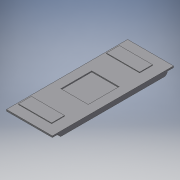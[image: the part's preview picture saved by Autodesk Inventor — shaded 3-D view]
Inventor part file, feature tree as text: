
AUTODESK INVENTOR PART (.ipt)
format: ipt  version: 2016 SP2 (Build 200236200, 236)  size: 184,320 bytes
history: native  units: mm
features: extrude x5, sketch x5, chamfer x1, reference x1
ambient origin geometry x8: Origin, YZ Plane, XZ Plane, XY Plane, X Axis, Y Axis, Z Axis, Center Point
bodies: Volumenkörper1 (feature_tree)
feature tree (12):
  extrude  "Extrusion1"  Depth=24.9mm
  extrude  "Extrusion2"  Depth=3.5mm
  extrude  "Extrusion3"  Depth=0.8mm TaperAngle=0.0deg
  chamfer  "Fase1"  Distance=7.0mm
  extrude  "Extrusion4"  Depth=7.0mm
  extrude  "Extrusion5"  Depth=5.5mm
  sketch  "Skizze1"  dims[d0=0.1mm d1=24.9mm]
  reference  "Referenz1"
  sketch  "Skizze2"  dims[d2=1.8mm d3=0.0mm d4=3.5mm]
  sketch  "Skizze3"  dims[d5=3.5mm d6=0.8mm d7=0.0mm]
  sketch  "Skizze4"  dims[d8=18.0mm]
  sketch  "Skizze5"  dims[d9=18.0mm d10=7.0mm d11=7.0mm d12=5.5mm d13=5.5mm d14=1.0mm d15=0.4mm d16=0.0mm d17=1.0mm d18=2.0mm d19=45.0deg d20=12.0mm d21=12.0mm d22=0.4mm d23=0.0mm d24=12.0mm d25=12.0mm d26=5.0mm d27=5.0mm d28=0.6mm d29=0.0mm]
